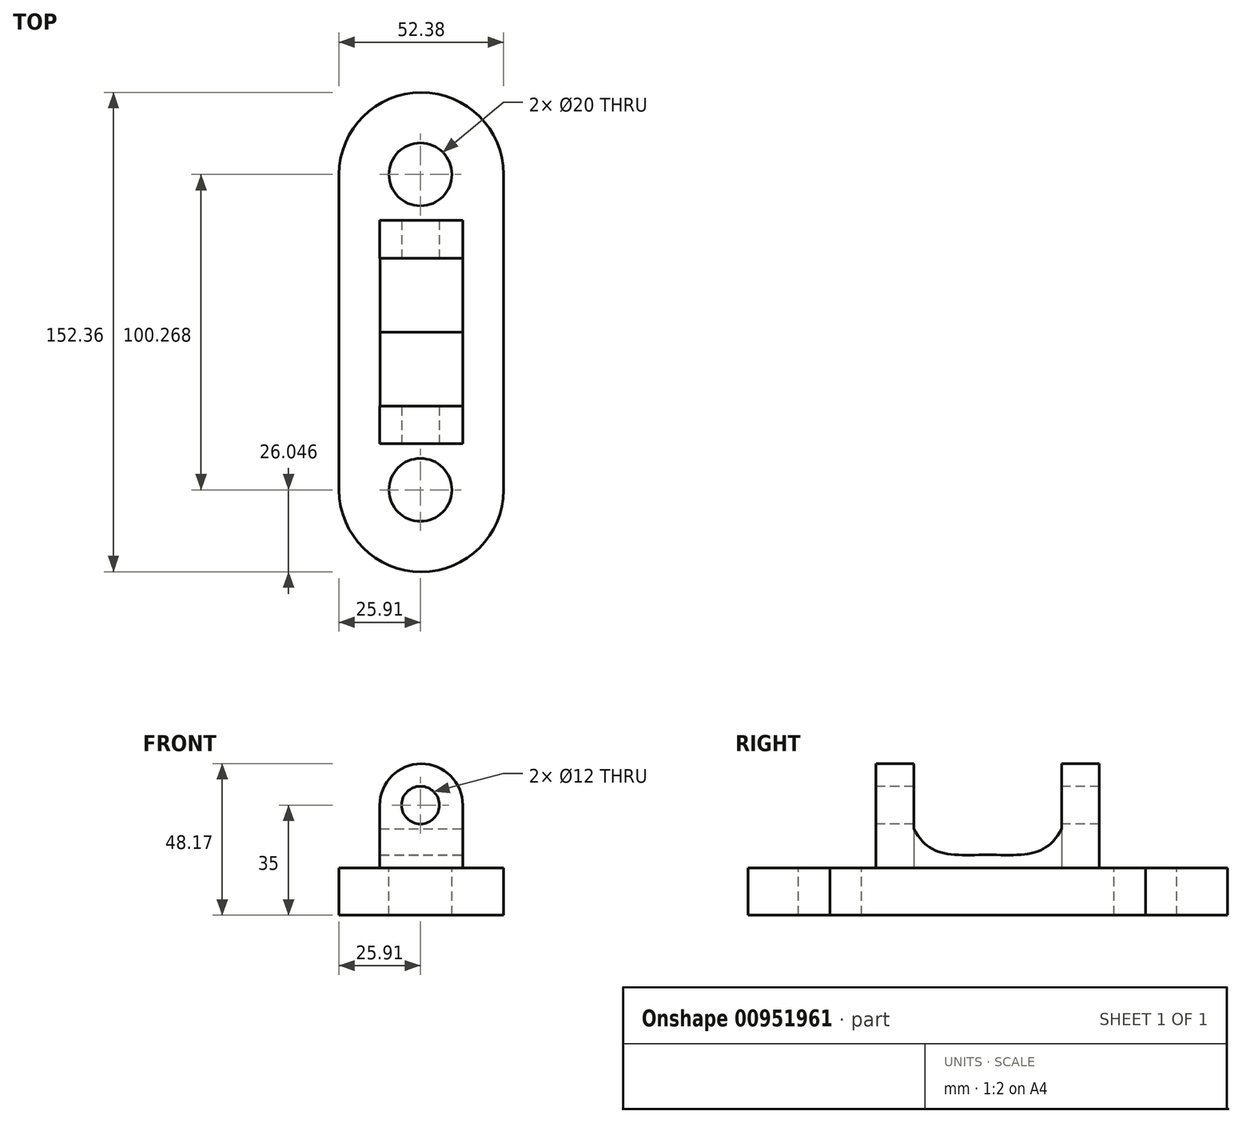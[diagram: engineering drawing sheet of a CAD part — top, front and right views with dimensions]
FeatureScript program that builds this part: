
annotation { "Feature Type Name" : "Feature", "Feature Type Description" : "" }
export const myFeature = defineFeature(function(context is Context, id is Id, definition is map)
    precondition{}
    {
        {
            var Q0;
            Q0=qCreatedBy(makeId("Top.planeOp"),FACE);
            var sketch = newSketch(context, id + "F0", { "sketchPlane" : qUnion([Q0])});
            skArc(sketch, "E0", {"start": v(26.47, 50.13) * mm, "mid": v(0.28, 76.18) * mm, "end": v(-25.9, 50.13) * mm});
            skLineSegment(sketch, "E1.bottom", {"start": v(-25.9, 50.13) * mm, "end": v(26.47, 50.13) * mm});
            skLineSegment(sketch, "E2.bottom", {"start": v(-25.9, 50.13) * mm, "end": v(26.44, 50.13) * mm});
            skLineSegment(sketch, "E2.top", {"start": v(-25.9, -49.97) * mm, "end": v(26.44, -49.97) * mm});
            skLineSegment(sketch, "E2.left", {"start": v(-25.9, 50.13) * mm, "end": v(-25.9, -49.97) * mm});
            skLineSegment(sketch, "E2.right", {"start": v(26.44, 50.13) * mm, "end": v(26.44, -49.97) * mm});
            skArc(sketch, "E3", {"start": v(-25.9, -49.97) * mm, "mid": v(0.27, -76.14) * mm, "end": v(26.44, -49.97) * mm});
            skSolve(sketch);
        }
        {
            var Q0;
            Q0 = qSketchRegion(id + "F0", true);
            extrude(context, id + "F1", {"entities" : qUnion([Q0]), "oppositeDirection" : true, "depth" : 15 * mm, "offsetDistance" : 25 * mm});
        }
        {
            var Q0;
            Q0=qCreatedBy(makeId("Top.planeOp"),FACE);
            var sketch = newSketch(context, id + "F2", { "sketchPlane" : qUnion([Q0])});
            skLineSegment(sketch, "E4.bottom", {"start": v(-12.9, -23.5) * mm, "end": v(13.44, -23.5) * mm});
            skLineSegment(sketch, "E4.top", {"start": v(-12.9, -35.5) * mm, "end": v(13.44, -35.5) * mm});
            skLineSegment(sketch, "E4.left", {"start": v(-12.9, -23.5) * mm, "end": v(-12.9, -35.5) * mm});
            skLineSegment(sketch, "E4.right", {"start": v(13.44, -23.5) * mm, "end": v(13.44, -35.5) * mm});
            skSolve(sketch);
        }
        {
            var Q0;
            Q0=makeQuery(id+"F2.imprint","IMPRINT",FACE,{"disambiguationData":[TD([[makeQuery(id+"F2.imprint","IMPRINT",EDGE,{"derivedFrom":sQuery(id+"F2.wireOp",EDGE,"E4.bottom")}),-1.0]])]});
            extrude(context, id + "F3", {"entities" : qUnion([Q0]), "operationType" : NewBodyOperationType.ADD, "depth" : 20 * mm, "offsetDistance" : 25 * mm});
        }
        {
            var Q0;
            Q0=makeQuery(id+"F3.opExtrude","SWEPT_FACE",FACE,{"disambiguationData":[OSD([sQuery(id+"F2.wireOp",EDGE,"E4.top")])]});
            var sketch = newSketch(context, id + "F4", { "sketchPlane" : qUnion([Q0])});
            skArc(sketch, "E5", {"start": v(13.44, 20) * mm, "mid": v(0.27, 33.17) * mm, "end": v(-12.9, 20) * mm});
            skSolve(sketch);
        }
        {
            var Q0;
            Q0=makeQuery(id+"F4.imprint","IMPRINT",FACE,{"disambiguationData":[TD([[makeQuery(id+"F4.imprint","IMPRINT",EDGE,{"derivedFrom":sQuery(id+"F4.wireOp",EDGE,"E5")}),1.0]])]});
            extrude(context, id + "F5", {"entities" : qUnion([Q0]), "operationType" : NewBodyOperationType.ADD, "oppositeDirection" : true, "depth" : 12 * mm, "offsetDistance" : 25 * mm});
        }
        {
            var Q0;
            Q0=makeQuery(id+"F3.opExtrude","SWEPT_FACE",FACE,{"disambiguationData":[OSD([sQuery(id+"F2.wireOp",EDGE,"E4.right")])]});
            var sketch = newSketch(context, id + "F6", { "sketchPlane" : qUnion([Q0])});
            skFitSpline(sketch, "E6", {"points": [v(-23.5, 12.53) * mm, v(-15.26, 5.1) * mm, v(0, 4.27) * mm], "startDerivative": vector(14.43, -27.42) * mm, "endDerivative": vector(33, 0.98) * mm});
            skLineSegment(sketch, "E7", {"start": v(0, 4.27) * mm, "end": v(0, 0) * mm});
            skLineSegment(sketch, "E8", {"start": v(0, 0) * mm, "end": v(-23.5, 0) * mm});
            skLineSegment(sketch, "E9", {"start": v(-23.5, 0) * mm, "end": v(-23.5, 12.53) * mm});
            skSolve(sketch);
        }
        {
            var Q0;
            {var subQ0=sQuery(id+"F6.wireOp",EDGE,"E7");Q0=makeQuery(id+"F6.imprint","IMPRINT",FACE,{"disambiguationData":[TD([[makeQuery(id+"F6.imprint","IMPRINT",EDGE,{"derivedFrom":subQ0}),-1.0]])]});}
            extrude(context, id + "F7", {"entities" : qUnion([Q0]), "operationType" : NewBodyOperationType.ADD, "oppositeDirection" : true, "depth" : 26.3 * mm, "offsetDistance" : 25 * mm});
        }
        {
            var Q0;
            Q0=makeQuery(id+"F1.opExtrude","SWEPT_BODY",BODY,{"disambiguationData":[OSD([sQuery(id+"F0.wireOp",EDGE,"E0"),sQuery(id+"F0.wireOp",EDGE,"E1.bottom"),sQuery(id+"F0.wireOp",EDGE,"E2.left"),sQuery(id+"F0.wireOp",EDGE,"E2.right"),sQuery(id+"F0.wireOp",EDGE,"E3")])]});
            var Q1;
            Q1=qCreatedBy(makeId("Front.planeOp"),FACE);
            mirror(context, id + "F8", {"operationType" : NewBodyOperationType.ADD, "entities" : qUnion([Q0]), "mirrorPlane" : qUnion([Q1])});
        }
        {
            var Q0;
            {var subQ0=sQuery(id+"F2.wireOp",EDGE,"E4.top");Q0=makeQuery(id+"F5.boolean.opBoolean","MERGE",FACE,{"derivedFrom":[makeQuery(id+"F3.opExtrude","SWEPT_FACE",FACE,{"disambiguationData":[OSD([subQ0])]}),makeQuery(id+"F5.opExtrude","CAP_FACE",FACE,{"disambiguationData":[OSD([subQ0,sQuery(id+"F4.wireOp",EDGE,"E5")])],"isStart":true})]});}
            var sketch = newSketch(context, id + "F9", { "sketchPlane" : qUnion([Q0])});
            skPoint(sketch, "E10", {"position": v(0, 20) * mm});
            skSolve(sketch);
        }
        {
            var Q0;
            Q0=sQuery(id+"F9.wireOp",VERTEX,"E10");
            var Q1;
            Q1=makeQuery(id+"F1.opExtrude","SWEPT_BODY",BODY,{"disambiguationData":[OSD([sQuery(id+"F0.wireOp",EDGE,"E0"),sQuery(id+"F0.wireOp",EDGE,"E1.bottom"),sQuery(id+"F0.wireOp",EDGE,"E2.left"),sQuery(id+"F0.wireOp",EDGE,"E2.right"),sQuery(id+"F0.wireOp",EDGE,"E3")])]});
            hole(context, id + "F10", {"style" : HoleStyle.SIMPLE, "endStyle" : HoleEndStyle.THROUGH, "holeDiameter" : 12 * mm, "majorDiameter" : 5 * mm, "isTappedThrough" : true, "tappedDepth" : 12 * mm, "tapClearance" : 3, "locations" : qUnion([Q0]), "scope" : qUnion([Q1])});
        }
        {
            var Q0;
            {var subQ0=makeQuery(id+"F1.opExtrude","CAP_FACE",FACE,{"disambiguationData":[OSD([sQuery(id+"F0.wireOp",EDGE,"E0"),sQuery(id+"F0.wireOp",EDGE,"E1.bottom"),sQuery(id+"F0.wireOp",EDGE,"E2.left"),sQuery(id+"F0.wireOp",EDGE,"E2.right"),sQuery(id+"F0.wireOp",EDGE,"E3")])],"isStart":true});Q0=makeQuery(id+"F8.boolean.opBoolean","MERGE",FACE,{"derivedFrom":[subQ0,makeQuery(id+"F8.opPattern","COPY",FACE,{"derivedFrom":subQ0,"instanceName":"1"})]});}
            var sketch = newSketch(context, id + "F11", { "sketchPlane" : qUnion([Q0])});
            skPoint(sketch, "E11", {"position": v(0, 50.13) * mm});
            skPoint(sketch, "E12", {"position": v(0, -50.13) * mm});
            skSolve(sketch);
        }
        {
            var Q0;
            Q0=sQuery(id+"F11.wireOp",VERTEX,"E11");
            var Q1;
            Q1=sQuery(id+"F11.wireOp",VERTEX,"E12");
            var Q2;
            Q2=makeQuery(id+"F1.opExtrude","SWEPT_BODY",BODY,{"disambiguationData":[OSD([sQuery(id+"F0.wireOp",EDGE,"E0"),sQuery(id+"F0.wireOp",EDGE,"E1.bottom"),sQuery(id+"F0.wireOp",EDGE,"E2.left"),sQuery(id+"F0.wireOp",EDGE,"E2.right"),sQuery(id+"F0.wireOp",EDGE,"E3")])]});
            hole(context, id + "F12", {"style" : HoleStyle.SIMPLE, "endStyle" : HoleEndStyle.THROUGH, "holeDiameter" : 20 * mm, "majorDiameter" : 5 * mm, "isTappedThrough" : true, "tappedDepth" : 12 * mm, "tapClearance" : 3, "locations" : qUnion([Q0, Q1]), "scope" : qUnion([Q2])});
        }
    });
